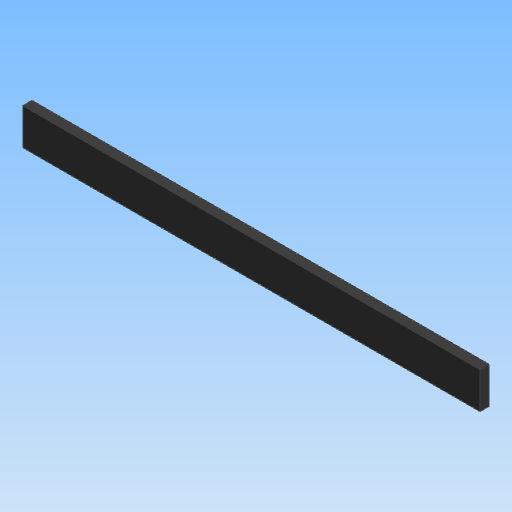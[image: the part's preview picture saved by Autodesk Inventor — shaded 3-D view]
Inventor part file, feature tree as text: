
AUTODESK INVENTOR PART (.ipt)
format: ipt  version: 2020 (Build 240168000, 168)  size: 94,720 bytes
history: native  units: mm
features: other x1, extrude x1
ambient origin geometry x8: Origin, YZ Plane, XZ Plane, XY Plane, X Axis, Y Axis, Z Axis, Center Point
bodies: Body1 (feature_tree)
feature tree (2):
  other  "實體1"
  extrude  "擠出1"  Depth=10.0mm
